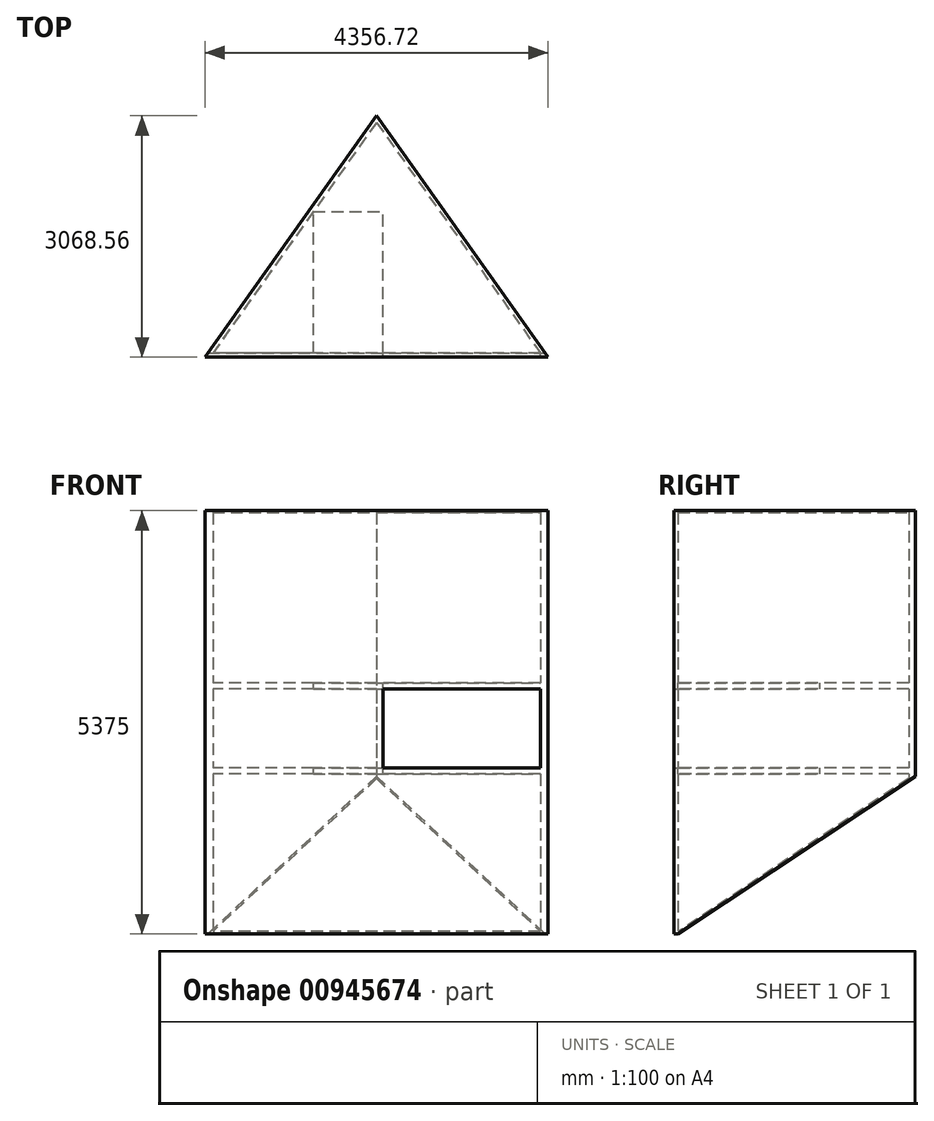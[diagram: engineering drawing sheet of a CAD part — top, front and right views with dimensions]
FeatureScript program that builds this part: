
annotation { "Feature Type Name" : "Feature", "Feature Type Description" : "" }
export const myFeature = defineFeature(function(context is Context, id is Id, definition is map)
    precondition{}
    {
        {
            var Q0;
            Q0=qCreatedBy(makeId("Top.planeOp"),FACE);
            var sketch = newSketch(context, id + "F0", { "sketchPlane" : qUnion([Q0])});
            skLineSegment(sketch, "E0", {"start": v(0, 0) * mm, "end": v(-2080, 0) * mm});
            skLineSegment(sketch, "E1", {"start": v(-2080, 0) * mm, "end": v(0, 2930) * mm});
            skLineSegment(sketch, "E2", {"start": v(0, 4272.57) * mm, "end": v(0, -958.59) * mm, "construction": true});
            skLineSegment(sketch, "E3.MirrorCS", {"start": v(2080, 0) * mm, "end": v(0, 2930) * mm});
            skLineSegment(sketch, "E4.MirrorCS", {"start": v(0, 0) * mm, "end": v(2080, 0) * mm});
            skLineSegment(sketch, "E5.0", {"start": v(-2178.36, -50.8) * mm, "end": v(0, 3017.76) * mm});
            skLineSegment(sketch, "E5.1", {"start": v(0, -50.8) * mm, "end": v(-2178.36, -50.8) * mm});
            skLineSegment(sketch, "E5.2", {"start": v(0, -50.8) * mm, "end": v(2178.36, -50.8) * mm});
            skLineSegment(sketch, "E5.3", {"start": v(2178.36, -50.8) * mm, "end": v(0, 3017.76) * mm});
            skSolve(sketch);
        }
        {
            var Q0;
            Q0 = qSketchRegion(id + "F0", true);
            extrude(context, id + "F1", {"entities" : qUnion([Q0]), "depth" : 5350 * mm, "offsetDistance" : 25 * mm});
        }
        {
            var Q0;
            Q0=qCreatedBy(makeId("Right.planeOp"),FACE);
            var sketch = newSketch(context, id + "F2", { "sketchPlane" : qUnion([Q0])});
            skLineSegment(sketch, "E6", {"start": v(0, 0) * mm, "end": v(3017.76, 2000) * mm});
            skLineSegment(sketch, "E7", {"start": v(3017.76, 2000) * mm, "end": v(3017.76, 0) * mm});
            skLineSegment(sketch, "E8", {"start": v(3017.76, 0) * mm, "end": v(0, 0) * mm});
            skSolve(sketch);
        }
        {
            var Q0;
            Q0 = qSketchRegion(id + "F2", true);
            var Q1;
            Q1=makeQuery(id+"F1.opExtrude","SWEPT_FACE",FACE,{"disambiguationData":[OSD([sQuery(id+"F0.wireOp",EDGE,"E5.3")])]});
            extrude(context, id + "F3", {"entities" : qUnion([Q0]), "operationType" : NewBodyOperationType.REMOVE, "endBound" : BoundingType.SYMMETRIC, "oppositeDirection" : true, "depth" : 5000 * mm, "offsetDistance" : 25 * mm, "hasSecondDirection" : true, "secondDirectionBound" : SecondDirectionBoundingType.UP_TO_SURFACE, "secondDirectionOppositeDirection" : false, "secondDirectionDepth" : 25 * mm, "secondDirectionBoundEntityFace" : qUnion([Q1])});
        }
        {
            var Q0;
            Q0=makeQuery(id+"F3.boolean.opBoolean","COPY",FACE,{"derivedFrom":makeQuery(id+"F3.opExtrude","SWEPT_FACE",FACE,{"disambiguationData":[OSD([sQuery(id+"F2.wireOp",EDGE,"E6")])]})});
            var sketch = newSketch(context, id + "F4", { "sketchPlane" : qUnion([Q0])});
            skLineSegment(sketch, "E9", {"start": v(0, -3620.34) * mm, "end": v(2142.3, 0) * mm});
            skLineSegment(sketch, "E10", {"start": v(2142.3, 0) * mm, "end": v(-2142.3, 0) * mm});
            skLineSegment(sketch, "E11", {"start": v(-2142.3, 0) * mm, "end": v(0, -3620.34) * mm});
            skSolve(sketch);
        }
        {
            var Q0;
            Q0 = qSketchRegion(id + "F4", true);
            extrude(context, id + "F5", {"entities" : qUnion([Q0]), "operationType" : NewBodyOperationType.ADD, "oppositeDirection" : true, "depth" : 25 * mm, "offsetDistance" : 25 * mm});
        }
        {
            var Q0;
            Q0=makeQuery(id+"F1.opExtrude","CAP_FACE",FACE,{"disambiguationData":[OSD([sQuery(id+"F0.wireOp",EDGE,"E0"),sQuery(id+"F0.wireOp",EDGE,"E1"),sQuery(id+"F0.wireOp",EDGE,"E3.MirrorCS"),sQuery(id+"F0.wireOp",EDGE,"E4.MirrorCS"),sQuery(id+"F0.wireOp",EDGE,"E5.0"),sQuery(id+"F0.wireOp",EDGE,"E5.1"),sQuery(id+"F0.wireOp",EDGE,"E5.2"),sQuery(id+"F0.wireOp",EDGE,"E5.3")])],"isStart":false});
            var sketch = newSketch(context, id + "F6", { "sketchPlane" : qUnion([Q0])});
            skLineSegment(sketch, "E12", {"start": v(0, 3017.76) * mm, "end": v(-2178.36, -50.8) * mm});
            skLineSegment(sketch, "E13", {"start": v(-2178.36, -50.8) * mm, "end": v(2178.36, -50.8) * mm});
            skLineSegment(sketch, "E14", {"start": v(2178.36, -50.8) * mm, "end": v(0, 3017.76) * mm});
            skSolve(sketch);
        }
        {
            var Q0;
            Q0 = qSketchRegion(id + "F6", true);
            extrude(context, id + "F7", {"entities" : qUnion([Q0]), "operationType" : NewBodyOperationType.ADD, "depth" : 25 * mm, "offsetDistance" : 25 * mm});
        }
        {
            var Q0;
            Q0=makeQuery(id+"F7.opExtrude","CAP_FACE",FACE,{"disambiguationData":[OSD([sQuery(id+"F6.wireOp",EDGE,"E12"),sQuery(id+"F6.wireOp",EDGE,"E13"),sQuery(id+"F6.wireOp",EDGE,"E14")])],"isStart":false});
            cPlane(context, id + "F8", {"entities" : qUnion([Q0]), "cplaneType" : CPlaneType.OFFSET, "offset" : 3000 * mm, "oppositeDirection" : true, "width" : 150 * mm, "height" : 150 * mm});
        }
        {
            var Q0;
            Q0=makeQuery(id+"F1.opExtrude","SWEPT_FACE",FACE,{"disambiguationData":[OSD([sQuery(id+"F0.wireOp",EDGE,"E0"),sQuery(id+"F0.wireOp",EDGE,"E4.MirrorCS")])]});
            var sketch = newSketch(context, id + "F9", { "sketchPlane" : qUnion([Q0])});
            skSolve(sketch);
        }
        {
            var Q0;
            {var subQ0=sQuery(id+"F0.wireOp",EDGE,"E0");Q0=makeQuery(id+"F9.imprint","IMPRINT",FACE,{"disambiguationData":[TD([[makeQuery(id+"F9.imprint","IMPRINT",EDGE,{"derivedFrom":makeQuery(id+"F1.opExtrude","SWEPT_EDGE",EDGE,{"disambiguationData":[OSD([subQ0,sQuery(id+"F0.wireOp",EDGE,"E1")])]})}),-1.0]])]});}
            var sketch = newSketch(context, id + "F10", { "sketchPlane" : qUnion([Q0])});
            skLineSegment(sketch, "E15.bottom", {"start": v(-2080, 3190) * mm, "end": v(2080, 3190) * mm});
            skLineSegment(sketch, "E15.top", {"start": v(-2080, 3110) * mm, "end": v(2080, 3110) * mm});
            skLineSegment(sketch, "E15.left", {"start": v(-2080, 3190) * mm, "end": v(-2080, 3110) * mm});
            skLineSegment(sketch, "E15.right", {"start": v(2080, 3190) * mm, "end": v(2080, 3110) * mm});
            skLineSegment(sketch, "E16.bottom", {"start": v(-2080, 2110) * mm, "end": v(2080, 2110) * mm});
            skLineSegment(sketch, "E16.top", {"start": v(-2080, 2030) * mm, "end": v(2080, 2030) * mm});
            skLineSegment(sketch, "E16.left", {"start": v(-2080, 2110) * mm, "end": v(-2080, 2030) * mm});
            skLineSegment(sketch, "E16.right", {"start": v(2080, 2110) * mm, "end": v(2080, 2030) * mm});
            skSolve(sketch);
        }
        {
            var Q0;
            Q0 = qSketchRegion(id + "F10", true);
            extrude(context, id + "F11", {"entities" : qUnion([Q0]), "operationType" : NewBodyOperationType.ADD, "endBound" : BoundingType.UP_TO_NEXT, "depth" : 25 * mm, "offsetDistance" : 25 * mm});
        }
        {
            var Q0;
            Q0=qCreatedBy(id+"F8.planeOp",FACE);
            var sketch = newSketch(context, id + "F12", { "sketchPlane" : qUnion([Q0])});
            skLineSegment(sketch, "E17.bottom", {"start": v(-802.18, 0) * mm, "end": v(80, 0) * mm});
            skLineSegment(sketch, "E17.top", {"start": v(-802.18, 1800) * mm, "end": v(80, 1800) * mm});
            skLineSegment(sketch, "E17.left", {"start": v(-802.18, 0) * mm, "end": v(-802.18, 1800) * mm});
            skLineSegment(sketch, "E17.right", {"start": v(80, 0) * mm, "end": v(80, 1800) * mm});
            skSolve(sketch);
        }
        {
            var Q0;
            Q0 = qSketchRegion(id + "F12", true);
            extrude(context, id + "F13", {"entities" : qUnion([Q0]), "operationType" : NewBodyOperationType.REMOVE, "oppositeDirection" : true, "depth" : 880 * mm, "offsetDistance" : 25 * mm, "hasSecondDirection" : true, "secondDirectionOppositeDirection" : false, "secondDirectionDepth" : 2000 * mm});
        }
        {
            var Q0;
            {var subQ0=sQuery(id+"F0.wireOp",EDGE,"E0");Q0=makeQuery(id+"F9.imprint","IMPRINT",FACE,{"disambiguationData":[TD([[makeQuery(id+"F9.imprint","IMPRINT",EDGE,{"derivedFrom":makeQuery(id+"F1.opExtrude","SWEPT_EDGE",EDGE,{"disambiguationData":[OSD([subQ0,sQuery(id+"F0.wireOp",EDGE,"E1")])]})}),-1.0]])]});}
            var sketch = newSketch(context, id + "F14", { "sketchPlane" : qUnion([Q0])});
            skLineSegment(sketch, "E18.bottom", {"start": v(-2080, 3110) * mm, "end": v(-80, 3110) * mm});
            skLineSegment(sketch, "E18.top", {"start": v(-2080, 2110) * mm, "end": v(-80, 2110) * mm});
            skLineSegment(sketch, "E18.left", {"start": v(-2080, 3110) * mm, "end": v(-2080, 2110) * mm});
            skLineSegment(sketch, "E18.right", {"start": v(-80, 3110) * mm, "end": v(-80, 2110) * mm});
            skSolve(sketch);
        }
        {
            var Q0;
            Q0 = qSketchRegion(id + "F14", true);
            extrude(context, id + "F15", {"entities" : qUnion([Q0]), "operationType" : NewBodyOperationType.REMOVE, "endBound" : BoundingType.UP_TO_NEXT, "oppositeDirection" : true, "depth" : 25 * mm, "offsetDistance" : 25 * mm});
        }
    });
